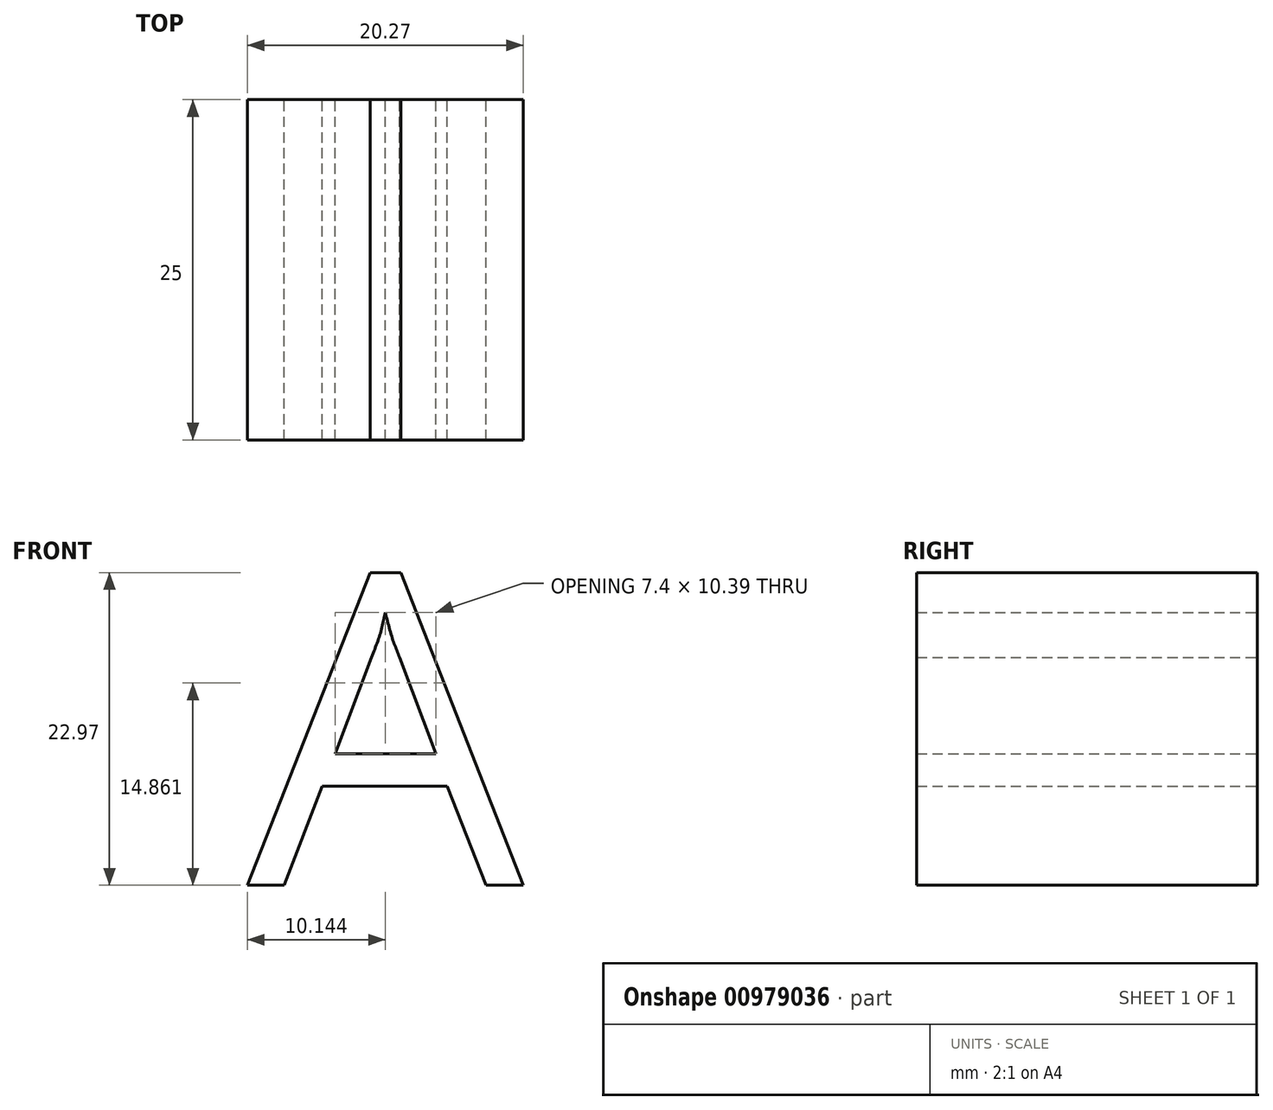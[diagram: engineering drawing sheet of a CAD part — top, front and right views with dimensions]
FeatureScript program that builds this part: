
annotation { "Feature Type Name" : "Feature", "Feature Type Description" : "" }
export const myFeature = defineFeature(function(context is Context, id is Id, definition is map)
    precondition{}
    {
        {
            var Q0;
            Q0=qCreatedBy(makeId("Front.planeOp"),FACE);
            var sketch = newSketch(context, id + "F0", { "sketchPlane" : qUnion([Q0])});
            skText(sketch, "E0", { "text": "A", "fontName": "OpenSans-Regular.ttf"});
            const initialGuessF0  = {"E0": [-0.07408, 0.01151, 1, 0, 0.02307]};
            skSetInitialGuess(sketch, initialGuessF0);
            skSolve(sketch);
        }
        {
            var Q0;
            Q0=qCreatedBy(makeId("Front.planeOp"),FACE);
            var sketch = newSketch(context, id + "F1", { "sketchPlane" : qUnion([Q0])});
            skLineSegment(sketch, "E1.0.0", {"start": v(-56.56, 11.51) * mm, "end": v(-53.8, 11.51) * mm});
            skLineSegment(sketch, "E1.0.1", {"start": v(-53.8, 11.51) * mm, "end": v(-62.8, 34.48) * mm});
            skLineSegment(sketch, "E1.0.2", {"start": v(-62.8, 34.48) * mm, "end": v(-65.04, 34.48) * mm});
            skLineSegment(sketch, "E1.0.3", {"start": v(-65.04, 34.48) * mm, "end": v(-74.08, 11.51) * mm});
            skLineSegment(sketch, "E1.0.4", {"start": v(-74.08, 11.51) * mm, "end": v(-71.39, 11.51) * mm});
            skLineSegment(sketch, "E1.0.5", {"start": v(-71.39, 11.51) * mm, "end": v(-68.58, 18.79) * mm});
            skLineSegment(sketch, "E1.0.6", {"start": v(-68.58, 18.79) * mm, "end": v(-59.41, 18.79) * mm});
            skLineSegment(sketch, "E1.0.7", {"start": v(-59.41, 18.79) * mm, "end": v(-56.56, 11.51) * mm});
            skLineSegment(sketch, "E2.0.0", {"start": v(-64.95, 28.27) * mm, "end": v(-67.63, 21.18) * mm});
            skLineSegment(sketch, "E2.0.1", {"start": v(-67.63, 21.18) * mm, "end": v(-60.24, 21.18) * mm});
            skLineSegment(sketch, "E2.0.2", {"start": v(-60.24, 21.18) * mm, "end": v(-62.9, 28.27) * mm});
            skFitSpline(sketch, "E2.0.3", {"points": [v(-62.9, 28.27) * mm, v(-63.42, 29.61) * mm, v(-63.96, 31.56) * mm]});
            skFitSpline(sketch, "E2.0.4", {"points": [v(-63.96, 31.56) * mm, v(-64.3, 30.06) * mm, v(-64.95, 28.27) * mm]});
            skSolve(sketch);
        }
        {
            var Q0;
            Q0 = qSketchRegion(id + "F1", true);
            extrude(context, id + "F2", {"entities" : qUnion([Q0]), "depth" : 25 * mm, "offsetDistance" : 25 * mm});
        }
    });
